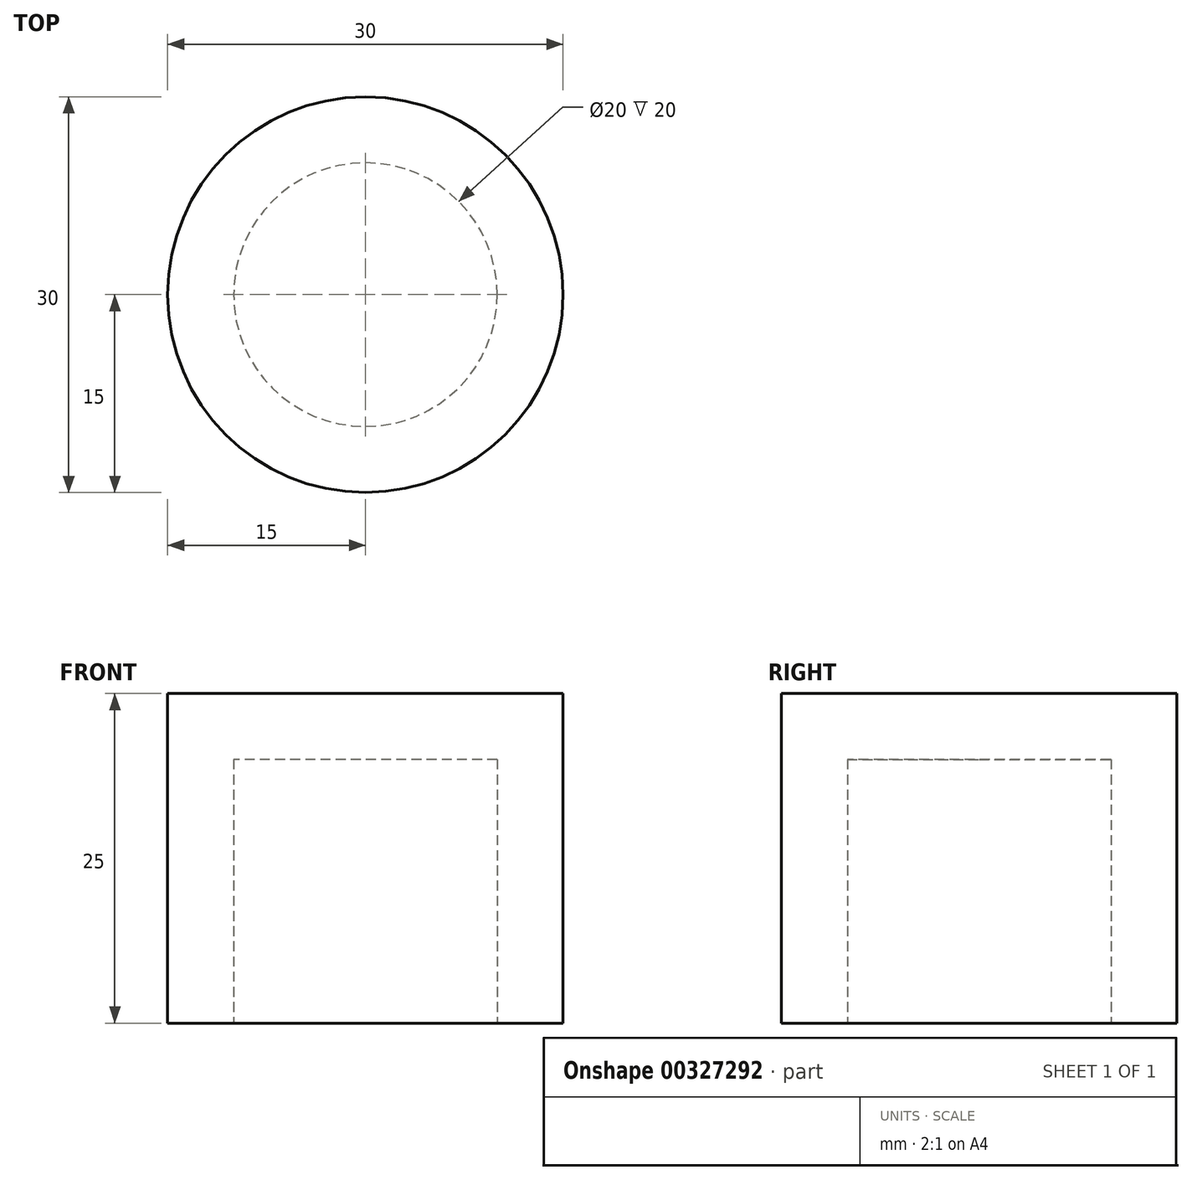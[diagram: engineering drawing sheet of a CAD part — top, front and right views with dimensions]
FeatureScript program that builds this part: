
annotation { "Feature Type Name" : "Feature", "Feature Type Description" : "" }
export const myFeature = defineFeature(function(context is Context, id is Id, definition is map)
    precondition{}
    {
        {
            var Q0;
            Q0=qCreatedBy(makeId("Top.planeOp"),FACE);
            var sketch = newSketch(context, id + "F0", { "sketchPlane" : qUnion([Q0])});
            skCircle(sketch, "E0", {"center": v(0, 0) * mm, "radius": 15 * mm});
            skCircle(sketch, "E1", {"center": v(0, 0) * mm, "radius": 10 * mm});
            skSolve(sketch);
        }
        {
            var Q0;
            Q0 = qSketchRegion(id + "F0", true);
            var Q1;
            Q1=makeQuery(id+"F0.imprint","IMPRINT",FACE,{"disambiguationData":[TD([[makeQuery(id+"F0.imprint","IMPRINT",EDGE,{"derivedFrom":sQuery(id+"F0.wireOp",EDGE,"E1")}),1.0]])]});
            extrude(context, id + "F1", {"entities" : qUnion([Q0, Q1]), "depth" : 25 * mm});
        }
        {
            var Q0;
            Q0=makeQuery(id+"F0.imprint","IMPRINT",FACE,{"disambiguationData":[TD([[makeQuery(id+"F0.imprint","IMPRINT",EDGE,{"derivedFrom":sQuery(id+"F0.wireOp",EDGE,"E1")}),1.0]])]});
            extrude(context, id + "F2", {"entities" : qUnion([Q0]), "operationType" : NewBodyOperationType.REMOVE, "depth" : 20 * mm});
        }
    });
